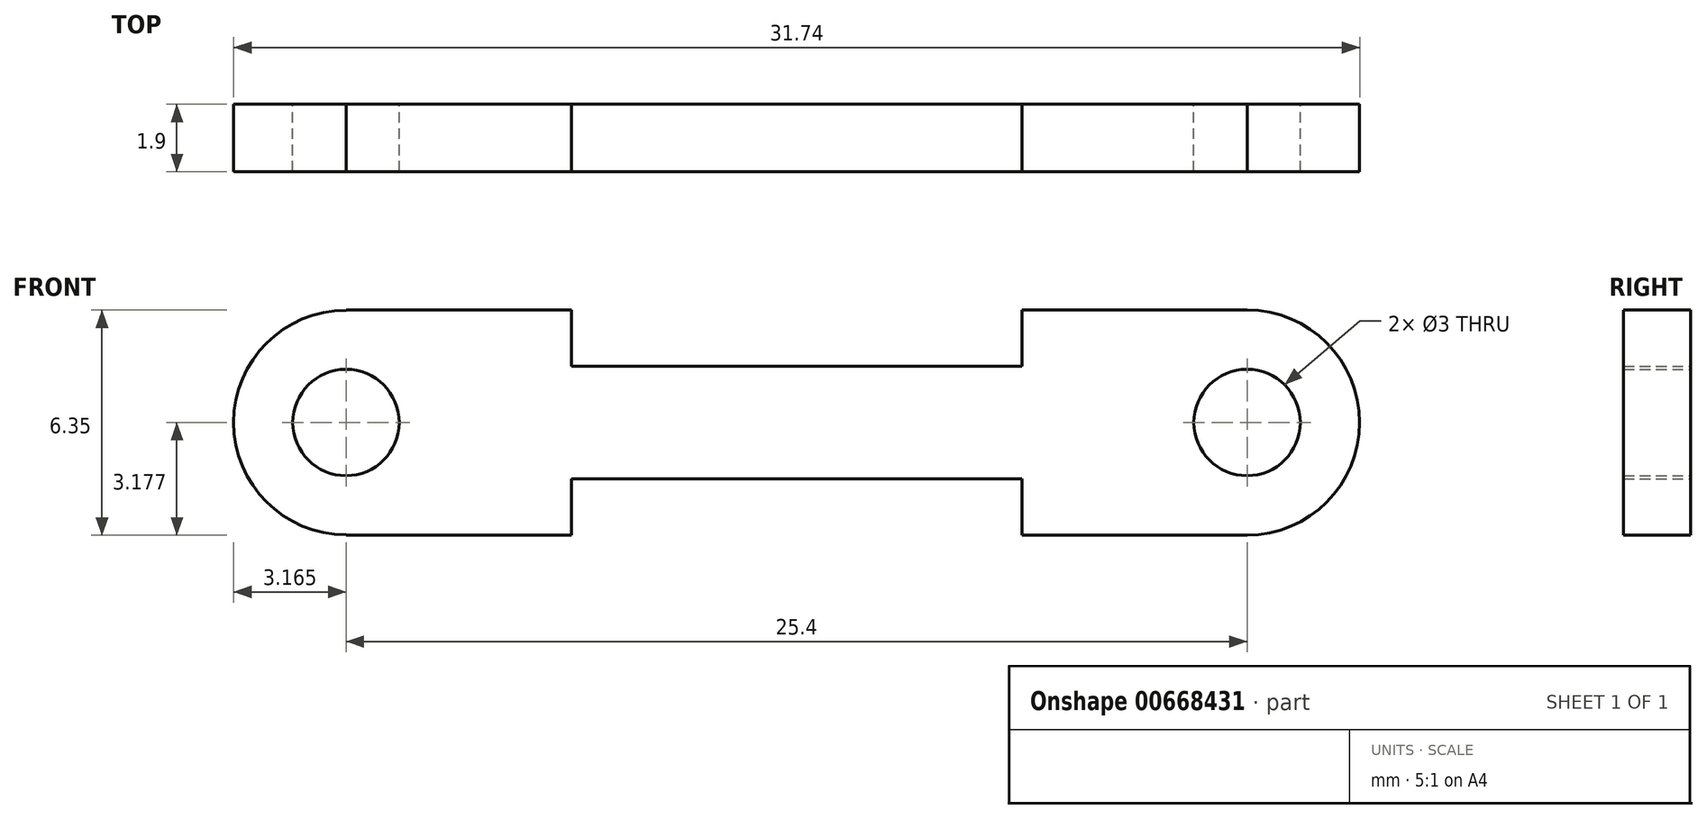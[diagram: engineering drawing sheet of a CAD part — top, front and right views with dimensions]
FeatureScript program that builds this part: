
annotation { "Feature Type Name" : "Feature", "Feature Type Description" : "" }
export const myFeature = defineFeature(function(context is Context, id is Id, definition is map)
    precondition{}
    {
        {
            var Q0;
            Q0=qCreatedBy(makeId("Front.planeOp"),FACE);
            var sketch = newSketch(context, id + "F0", { "sketchPlane" : qUnion([Q0])});
            skPoint(sketch, "E0", {"position": v(-48.06, 44.23) * mm});
            skPoint(sketch, "E1", {"position": v(-48.06, 37.88) * mm});
            skLineSegment(sketch, "E2", {"start": v(-41.7, 44.23) * mm, "end": v(-41.7, 42.64) * mm});
            skLineSegment(sketch, "E3", {"start": v(-54.4, 42.64) * mm, "end": v(-54.4, 44.23) * mm});
            skLineSegment(sketch, "E4", {"start": v(-54.4, 44.23) * mm, "end": v(-54.4, 42.64) * mm});
            skLineSegment(sketch, "E5", {"start": v(-54.4, 42.64) * mm, "end": v(-41.7, 42.64) * mm});
            skLineSegment(sketch, "E6", {"start": v(-41.7, 37.88) * mm, "end": v(-41.7, 39.47) * mm});
            skLineSegment(sketch, "E7", {"start": v(-41.7, 39.47) * mm, "end": v(-54.4, 39.47) * mm});
            skLineSegment(sketch, "E8", {"start": v(-54.4, 39.47) * mm, "end": v(-54.4, 37.88) * mm});
            skLineSegment(sketch, "E9", {"start": v(-35.36, 44.23) * mm, "end": v(-41.7, 44.23) * mm});
            skLineSegment(sketch, "E10", {"start": v(-35.36, 37.88) * mm, "end": v(-41.7, 37.88) * mm});
            skCircle(sketch, "E11.MirrorC", {"center": v(-35.36, 41.06) * mm, "radius": 1.5 * mm});
            skLineSegment(sketch, "E12", {"start": v(-35.36, 44.23) * mm, "end": v(-35.36, 44.23) * mm});
            skArc(sketch, "E13", {"start": v(-35.36, 37.88) * mm, "mid": v(-32.18, 41.06) * mm, "end": v(-35.36, 44.23) * mm});
            skLineSegment(sketch, "E14.trimOffspring", {"start": v(-35.36, 37.88) * mm, "end": v(-35.36, 37.88) * mm});
            skLineSegment(sketch, "E15", {"start": v(-54.4, 37.88) * mm, "end": v(-60.76, 37.88) * mm});
            skLineSegment(sketch, "E16", {"start": v(-54.4, 44.23) * mm, "end": v(-60.76, 44.23) * mm});
            skLineSegment(sketch, "E17", {"start": v(-60.76, 44.23) * mm, "end": v(-60.76, 44.22) * mm});
            skArc(sketch, "E18", {"start": v(-60.76, 44.22) * mm, "mid": v(-63.92, 41.06) * mm, "end": v(-60.76, 37.89) * mm});
            skLineSegment(sketch, "E19.trimOffspring", {"start": v(-60.76, 37.89) * mm, "end": v(-60.76, 37.88) * mm});
            skCircle(sketch, "E20", {"center": v(-60.76, 41.06) * mm, "radius": 1.5 * mm});
            skSolve(sketch);
        }
        {
            var Q0;
            Q0=makeQuery(id+"F0.imprint","IMPRINT",FACE,{"disambiguationData":[TD([[makeQuery(id+"F0.imprint","IMPRINT",EDGE,{"derivedFrom":sQuery(id+"F0.wireOp",EDGE,"E2")}),1.0]])]});
            extrude(context, id + "F1", {"entities" : qUnion([Q0]), "depth" : 1.9 * mm});
        }
    });
